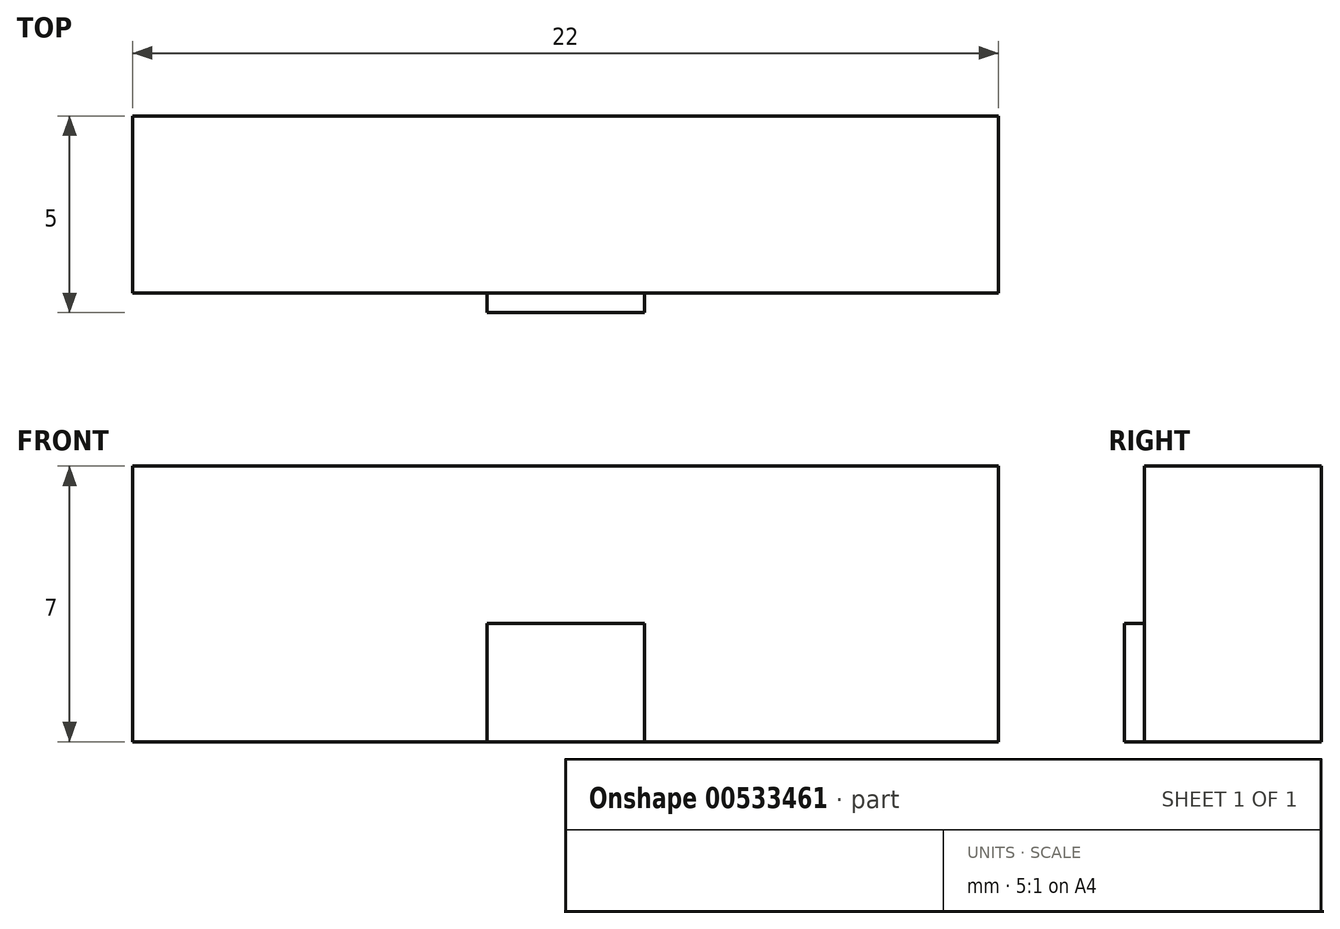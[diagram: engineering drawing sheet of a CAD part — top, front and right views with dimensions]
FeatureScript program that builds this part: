
annotation { "Feature Type Name" : "Feature", "Feature Type Description" : "" }
export const myFeature = defineFeature(function(context is Context, id is Id, definition is map)
    precondition{}
    {
        {
            var Q0;
            Q0=qCreatedBy(makeId("Top.planeOp"),FACE);
            var sketch = newSketch(context, id + "F0", { "sketchPlane" : qUnion([Q0])});
            skLineSegment(sketch, "E0.bottom", {"start": v(0, 0) * mm, "end": v(22, 0) * mm});
            skLineSegment(sketch, "E0.top", {"start": v(0, 4.5) * mm, "end": v(22, 4.5) * mm});
            skLineSegment(sketch, "E0.left", {"start": v(0, 0) * mm, "end": v(0, 4.5) * mm});
            skLineSegment(sketch, "E0.right", {"start": v(22, 0) * mm, "end": v(22, 4.5) * mm});
            skSolve(sketch);
        }
        {
            var Q0;
            Q0 = qSketchRegion(id + "F0", true);
            extrude(context, id + "F1", {"entities" : qUnion([Q0]), "depth" : 7 * mm, "offsetDistance" : 25 * mm});
        }
        {
            var Q0;
            Q0=makeQuery(id+"F1.opExtrude","SWEPT_FACE",FACE,{"disambiguationData":[OSD([sQuery(id+"F0.wireOp",EDGE,"E0.bottom")])]});
            var sketch = newSketch(context, id + "F2", { "sketchPlane" : qUnion([Q0])});
            skLineSegment(sketch, "E1.bottom", {"start": v(9, 0) * mm, "end": v(13, 0) * mm});
            skLineSegment(sketch, "E1.top", {"start": v(9, 3) * mm, "end": v(13, 3) * mm});
            skLineSegment(sketch, "E1.left", {"start": v(9, 0) * mm, "end": v(9, 3) * mm});
            skLineSegment(sketch, "E1.right", {"start": v(13, 0) * mm, "end": v(13, 3) * mm});
            skSolve(sketch);
        }
        {
            var Q0;
            Q0 = qSketchRegion(id + "F2", true);
            extrude(context, id + "F3", {"entities" : qUnion([Q0]), "operationType" : NewBodyOperationType.ADD, "depth" : 0.5 * mm, "offsetDistance" : 25 * mm});
        }
    });
